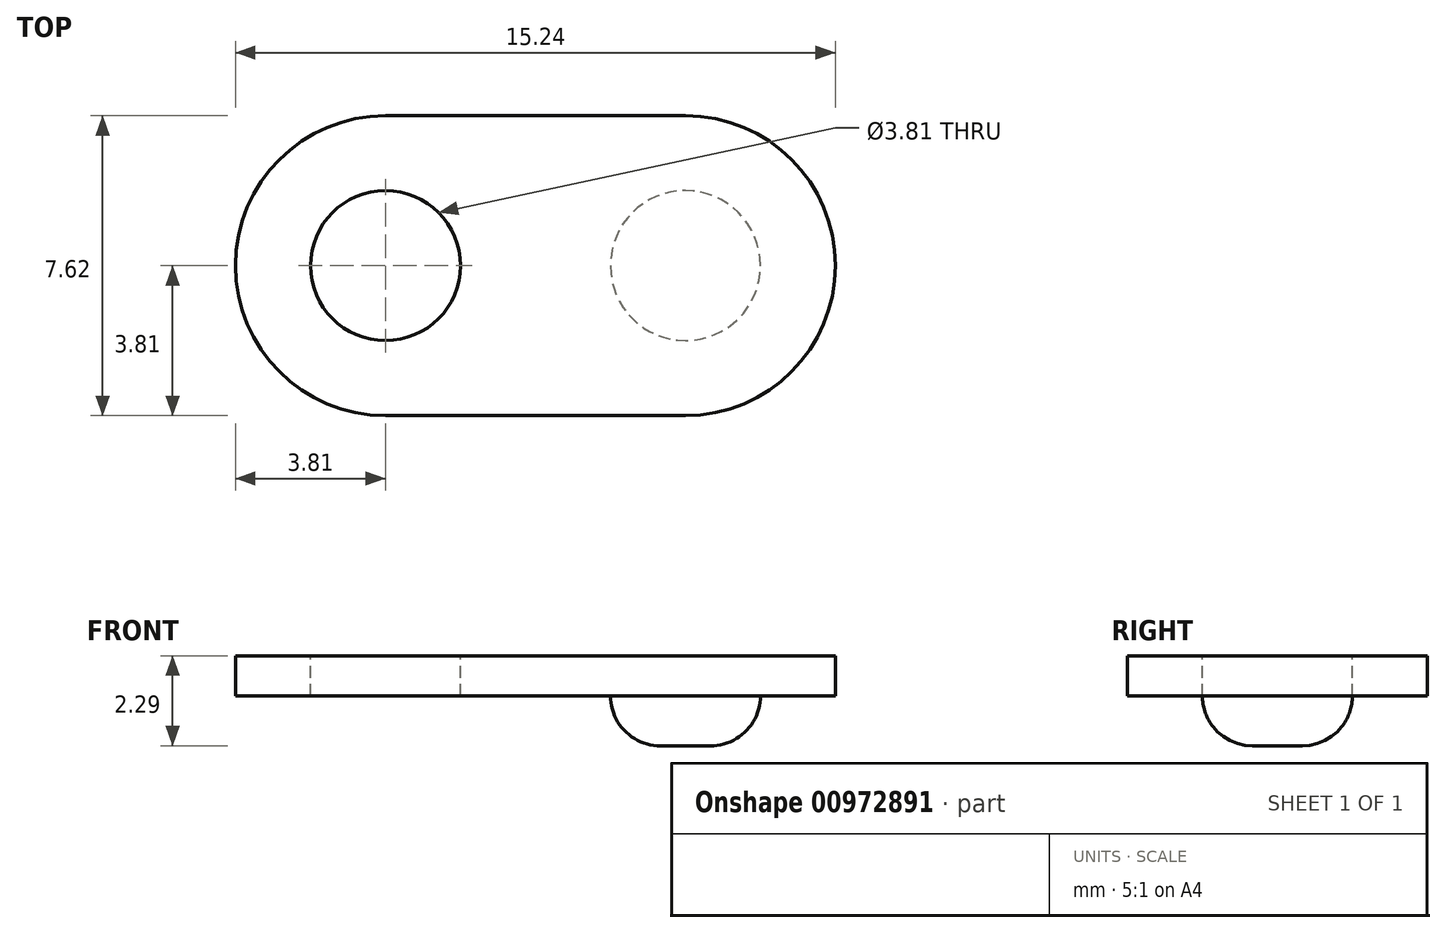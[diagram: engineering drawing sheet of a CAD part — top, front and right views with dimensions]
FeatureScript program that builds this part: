
annotation { "Feature Type Name" : "Feature", "Feature Type Description" : "" }
export const myFeature = defineFeature(function(context is Context, id is Id, definition is map)
    precondition{}
    {
        {
            var Q0;
            Q0=qCreatedBy(makeId("Top.planeOp"),FACE);
            var sketch = newSketch(context, id + "F0", { "sketchPlane" : qUnion([Q0])});
            skPoint(sketch, "E0", {"position": v(3.81, 0) * mm});
            skPoint(sketch, "E1", {"position": v(-3.8, 0) * mm});
            skCircle(sketch, "E2", {"center": v(3.81, 0) * mm, "radius": 3.81 * mm});
            skCircle(sketch, "E3", {"center": v(-3.8, 0) * mm, "radius": 3.81 * mm});
            skLineSegment(sketch, "E4", {"start": v(-3.8, 3.81) * mm, "end": v(3.81, 3.81) * mm});
            skLineSegment(sketch, "E5", {"start": v(-3.8, -3.8) * mm, "end": v(3.81, -3.81) * mm});
            skSolve(sketch);
        }
        {
            var Q0;
            Q0 = qSketchRegion(id + "F0", true);
            var Q1;
            {var subQ0=sQuery(id+"F0.wireOp",EDGE,"E3");var subQ1=sQuery(id+"F0.wireOp",EDGE,"E2");var subQ2=makeQuery(id+"F0.imprint","INTERSECT",VERTEX,{"disambiguationData":[OD(0.0)],"derivedFrom":[subQ1,subQ0]});Q1=makeQuery(id+"F0.imprint","IMPRINT",FACE,{"disambiguationData":[TD([[makeQuery(id+"F0.imprint","IMPRINT",EDGE,{"disambiguationData":[TD([[subQ2,-1.0]])],"derivedFrom":subQ1}),1.0]])]});}
            extrude(context, id + "F1", {"entities" : qUnion([Q0, Q1]), "depth" : 1.02 * mm, "offsetDistance" : 25.4 * mm});
        }
        {
            var Q0;
            Q0=makeQuery(id+"F1.opExtrude","CAP_FACE",FACE,{"disambiguationData":[OSD([sQuery(id+"F0.wireOp",EDGE,"E2"),sQuery(id+"F0.wireOp",EDGE,"E3"),sQuery(id+"F0.wireOp",EDGE,"E4"),sQuery(id+"F0.wireOp",EDGE,"E5")])],"isStart":false});
            var sketch = newSketch(context, id + "F2", { "sketchPlane" : qUnion([Q0])});
            skPoint(sketch, "E6", {"position": v(-3.8, 0) * mm});
            skSolve(sketch);
        }
        {
            var Q0;
            Q0=sQuery(id+"F2.wireOp",VERTEX,"E6");
            var Q1;
            Q1=makeQuery(id+"F1.opExtrude","SWEPT_BODY",BODY,{"disambiguationData":[OSD([sQuery(id+"F0.wireOp",EDGE,"E2"),sQuery(id+"F0.wireOp",EDGE,"E3"),sQuery(id+"F0.wireOp",EDGE,"E4"),sQuery(id+"F0.wireOp",EDGE,"E5")])]});
            hole(context, id + "F3", {"style" : HoleStyle.SIMPLE, "endStyle" : HoleEndStyle.THROUGH, "holeDiameter" : 3.8 * mm, "majorDiameter" : 6.35 * mm, "isTappedThrough" : true, "tappedDepth" : 12.7 * mm, "tapClearance" : 3, "locations" : qUnion([Q0]), "scope" : qUnion([Q1])});
        }
        {
            var Q0;
            Q0=makeQuery(id+"F1.opExtrude","CAP_FACE",FACE,{"disambiguationData":[OSD([sQuery(id+"F0.wireOp",EDGE,"E2"),sQuery(id+"F0.wireOp",EDGE,"E3"),sQuery(id+"F0.wireOp",EDGE,"E4"),sQuery(id+"F0.wireOp",EDGE,"E5")])],"isStart":true});
            var sketch = newSketch(context, id + "F4", { "sketchPlane" : qUnion([Q0])});
            skPoint(sketch, "E7", {"position": v(3.81, 0) * mm});
            skCircle(sketch, "E8", {"center": v(3.81, 0) * mm, "radius": 1.9 * mm});
            skSolve(sketch);
        }
        {
            var Q0;
            Q0=makeQuery(id+"F4.imprint","IMPRINT",FACE,{"disambiguationData":[TD([[makeQuery(id+"F4.imprint","IMPRINT",EDGE,{"derivedFrom":sQuery(id+"F4.wireOp",EDGE,"E8")}),1.0]])]});
            extrude(context, id + "F5", {"entities" : qUnion([Q0]), "operationType" : NewBodyOperationType.ADD, "depth" : 1.27 * mm, "offsetDistance" : 25.4 * mm});
        }
        {
            var Q0;
            Q0=makeQuery(id+"F5.opExtrude","CAP_EDGE",EDGE,{"disambiguationData":[OSD([sQuery(id+"F4.wireOp",EDGE,"E8")])],"isStart":false});
            fillet(context, id + "F6", {"entities" : qUnion([Q0]), "radius" : 1.27 * mm, "tangentPropagation" : true, "allowEdgeOverflow" : false});
        }
    });
